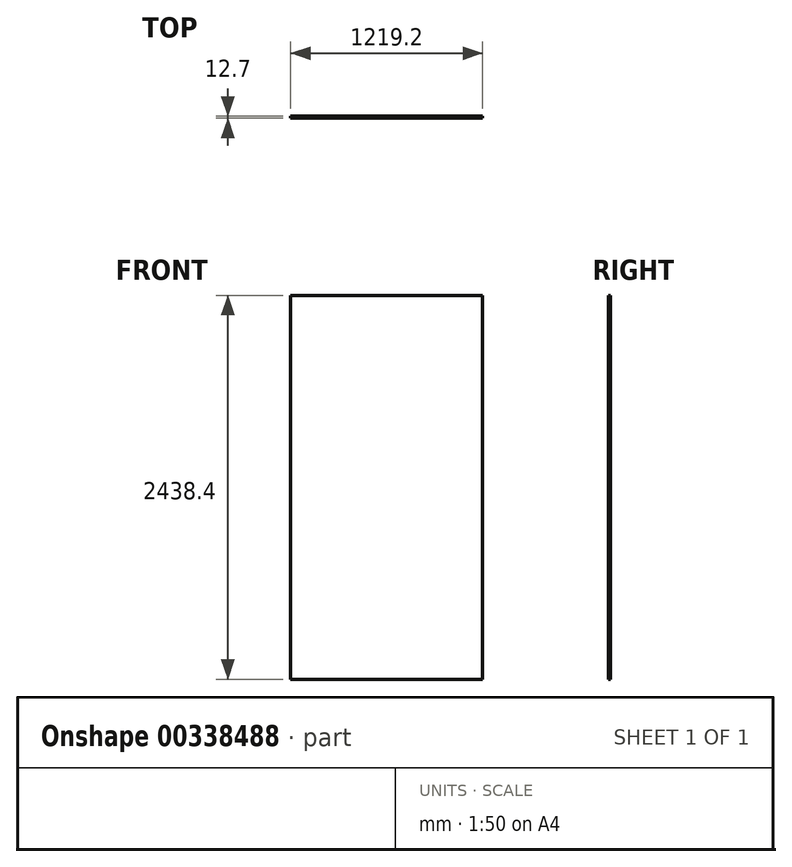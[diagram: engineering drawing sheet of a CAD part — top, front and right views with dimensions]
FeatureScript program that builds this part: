
annotation { "Feature Type Name" : "Feature", "Feature Type Description" : "" }
export const myFeature = defineFeature(function(context is Context, id is Id, definition is map)
    precondition{}
    {
        {
            var Q0;
            Q0=qCreatedBy(makeId("Front.planeOp"),FACE);
            var sketch = newSketch(context, id + "F0", { "sketchPlane" : qUnion([Q0])});
            skLineSegment(sketch, "E0.bottom", {"start": v(-609.6, 1219.2) * mm, "end": v(609.6, 1219.2) * mm});
            skLineSegment(sketch, "E0.top", {"start": v(-609.6, -1219.2) * mm, "end": v(609.6, -1219.2) * mm});
            skLineSegment(sketch, "E0.left", {"start": v(-609.6, 1219.2) * mm, "end": v(-609.6, -1219.2) * mm});
            skLineSegment(sketch, "E0.right", {"start": v(609.6, 1219.2) * mm, "end": v(609.6, -1219.2) * mm});
            skPoint(sketch, "E0.middle", {"position": v(0, 0) * mm});
            skSolve(sketch);
        }
        {
            var Q0;
            Q0=makeQuery(id+"F0.imprint","IMPRINT",FACE,{"disambiguationData":[TD([[makeQuery(id+"F0.imprint","IMPRINT",EDGE,{"derivedFrom":sQuery(id+"F0.wireOp",EDGE,"E0.bottom")}),-1.0]])]});
            extrude(context, id + "F1", {"entities" : qUnion([Q0]), "depth" : 12.7 * mm});
        }
    });
